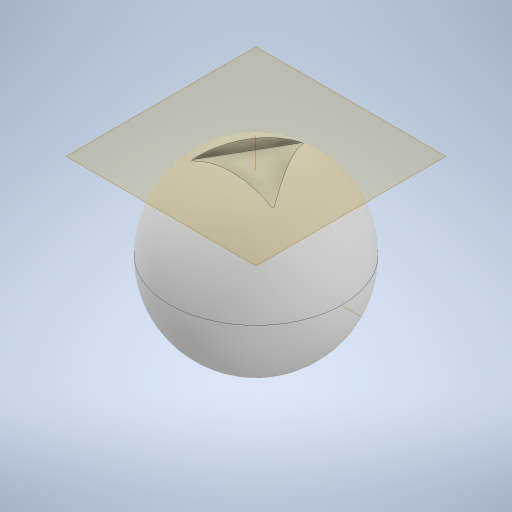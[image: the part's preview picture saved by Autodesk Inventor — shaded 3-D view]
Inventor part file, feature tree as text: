
AUTODESK INVENTOR PART (.ipt)
format: ipt  version: 2023 (Build 270158030, 158C)  size: 295,424 bytes
history: native  units: mm
features: plane x7, sketch x3, extrude x2, revolve x1, pattern_circular x1
ambient origin geometry x8: Origin, YZ Plane, XZ Plane, XY Plane, X Axis, Y Axis, Z Axis, Center Point
bodies: Solid1 (feature_tree)
feature tree (14):
  revolve  "Revolution1"  Angle=180.0deg
  plane  "Work Plane16"
  extrude  "Extrusion2"  TaperAngle=45.0deg  [1 undecoded]
  pattern_circular  "Circular Pattern4"  [2 undecoded]
  plane  "Work Plane10"
  plane  "Work Plane11"
  plane  "Work Plane12"
  plane  "Work Plane13"
  plane  "Work Plane14"
  plane  "Work Plane15"
  extrude  "Extrusion1"  Depth=7.0mm
  sketch  "Sketch1"  dims[d0=50.0mm d1=180.0deg]
  sketch  "Sketch2"  dims[d2=24.0mm d3=45.0deg]
  sketch  "Sketch3"  dims[d4=0.0mm d5=10.0mm d6=0.0mm d16=7.0mm d17=4.0mm d18=0.0mm d19=20.0mm d20=180.0deg d7=0.5mm d8=0.872665mm]
note: 3 required parameter values undecoded (feature->parameter linkage not recoverable at this tier; creation-order binding heuristic only, values carry confidence <= 0.55)
